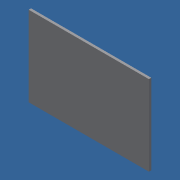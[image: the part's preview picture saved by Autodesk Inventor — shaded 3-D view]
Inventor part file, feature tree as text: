
AUTODESK INVENTOR PART (.ipt)
format: ipt  version: 2021 (Build 250183000, 183)  size: 76,800 bytes
history: native  units: mm
features: other x1, extrude x1, sketch x1
ambient origin geometry x8: Origin, YZ Plane, XZ Plane, XY Plane, X Axis, Y Axis, Z Axis, Center Point
bodies: Solid1 (feature_tree)
feature tree (3):
  other  "<userpath>\OneDrive\Objet3D\3DPrinter\Parameters.xlsx"
  extrude  "Extrusion1"  Depth=200.0mm
  sketch  "Sketch1"  dims[d0=6.0mm d1=0.0mm d2=200.0mm d3=300.0mm]
